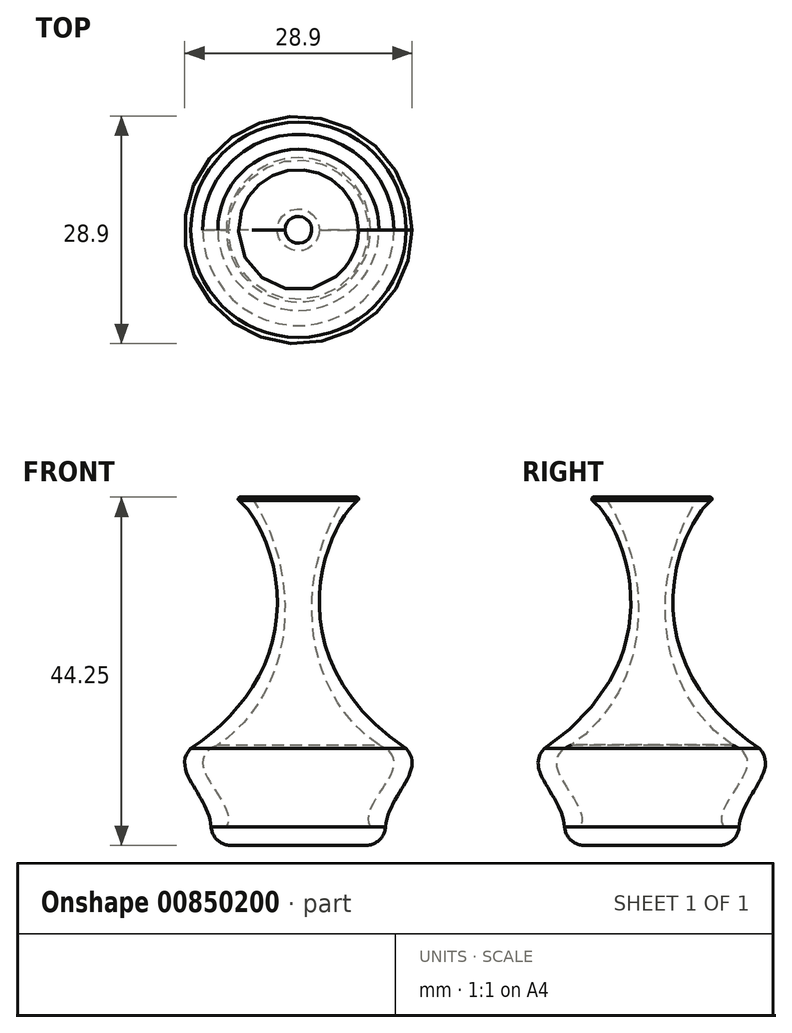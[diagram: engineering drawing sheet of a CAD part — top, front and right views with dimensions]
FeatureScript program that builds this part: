
annotation { "Feature Type Name" : "Feature", "Feature Type Description" : "" }
export const myFeature = defineFeature(function(context is Context, id is Id, definition is map)
    precondition{}
    {
        {
            var Q0;
            Q0=qCreatedBy(makeId("Right.planeOp"),FACE);
            var sketch = newSketch(context, id + "F0", { "sketchPlane" : qUnion([Q0])});
            skLineSegment(sketch, "E0", {"start": v(0, 0) * mm, "end": v(-11.45, 0) * mm});
            skFitSpline(sketch, "E1", {"points": [v(-11.45, 0) * mm, v(-13.67, 12.3) * mm], "startDerivative": vector(6.38, 15.68) * mm, "endDerivative": vector(9.38, 9.88) * mm});
            skLineSegment(sketch, "E2", {"start": v(-8.4, 44.25) * mm, "end": v(0, 44.25) * mm});
            skLineSegment(sketch, "E3", {"start": v(0, 44.25) * mm, "end": v(0, 0) * mm});
            skFitSpline(sketch, "E4", {"points": [v(-8.4, 44.25) * mm, v(-13.67, 12.3) * mm], "startDerivative": vector(11.06, -2.72) * mm, "endDerivative": vector(-55.27, -37.3) * mm});
            skSolve(sketch);
        }
        {
            var Q0;
            Q0 = qSketchRegion(id + "F0", true);
            var Q1;
            Q1=sQuery(id+"F0.wireOp",EDGE,"E3");
            revolve(context, id + "F1", {"surfaceOperationType" : NewSurfaceOperationType.NEW, "entities" : qUnion([Q0]), "axis" : qUnion([Q1]), "revolveType" : RevolveType.FULL});
        }
        {
            var Q0;
            Q0=makeQuery(id+"F1.opRevolve","SWEPT_FACE",FACE,{"disambiguationData":[OSD([sQuery(id+"F0.wireOp",EDGE,"E0")])]});
            fillet(context, id + "F2", {"entities" : qUnion([Q0]), "radius" : 2.54 * mm, "tangentPropagation" : true, "allowEdgeOverflow" : false});
        }
        {
            var Q0;
            Q0=qCreatedBy(makeId("Right.planeOp"),FACE);
            var sketch = newSketch(context, id + "F3", { "sketchPlane" : qUnion([Q0])});
            skFitSpline(sketch, "E5", {"points": [v(7.69, 46.62) * mm, v(10.23, 12.75) * mm], "startDerivative": vector(-26.73, -32.3) * mm, "endDerivative": vector(30.7, -20.63) * mm});
            skFitSpline(sketch, "E6", {"points": [v(10.23, 12.75) * mm, v(9.16, 2.37) * mm], "startDerivative": vector(16.74, -6.75) * mm, "endDerivative": vector(5.58, -8.81) * mm});
            skLineSegment(sketch, "E7", {"start": v(9.16, 2.37) * mm, "end": v(0, 2.37) * mm});
            skLineSegment(sketch, "E8", {"start": v(7.69, 46.62) * mm, "end": v(0, 46.62) * mm});
            skLineSegment(sketch, "E9", {"start": v(0, 46.62) * mm, "end": v(0, 2.37) * mm});
            skSolve(sketch);
        }
        {
            var Q0;
            Q0 = qSketchRegion(id + "F3", true);
            var Q1;
            Q1=sQuery(id+"F3.wireOp",EDGE,"E9");
            revolve(context, id + "F4", {"operationType" : NewBodyOperationType.REMOVE, "surfaceOperationType" : NewSurfaceOperationType.NEW, "entities" : qUnion([Q0]), "axis" : qUnion([Q1]), "revolveType" : RevolveType.FULL, "oppositeDirection" : true});
        }
        {
            var Q0;
            Q0=makeQuery(id+"F1.opRevolve","SWEPT_FACE",FACE,{"disambiguationData":[OSD([sQuery(id+"F0.wireOp",EDGE,"E2")])]});
            fillet(context, id + "F5", {"entities" : qUnion([Q0]), "radius" : 0.25 * mm, "tangentPropagation" : true, "allowEdgeOverflow" : false});
        }
    });
